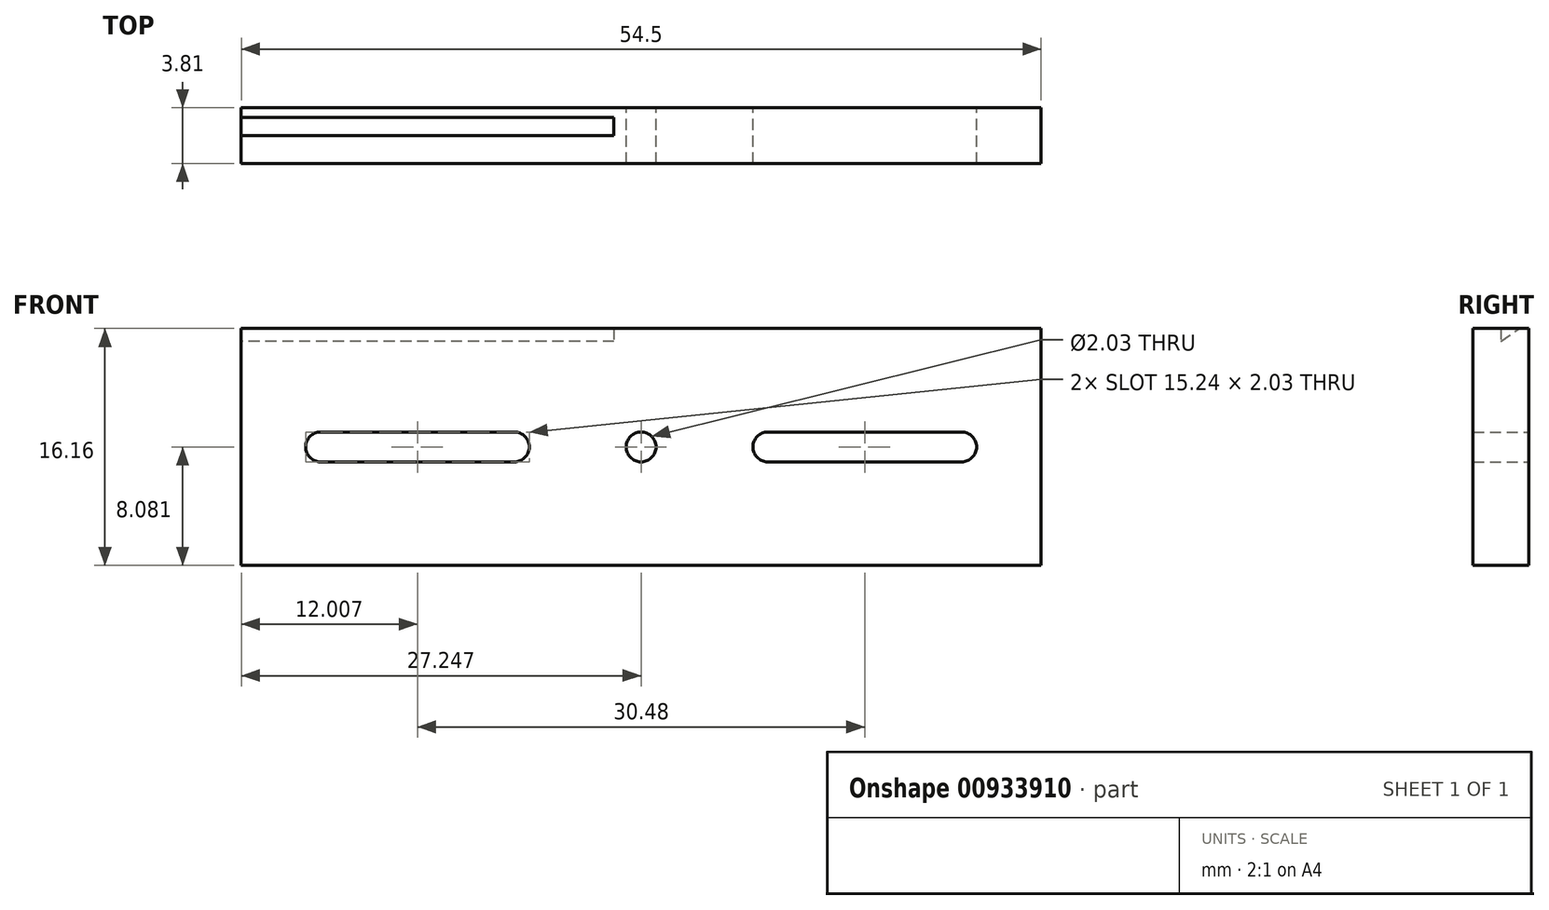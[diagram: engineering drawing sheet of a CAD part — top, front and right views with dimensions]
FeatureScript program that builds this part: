
annotation { "Feature Type Name" : "Feature", "Feature Type Description" : "" }
export const myFeature = defineFeature(function(context is Context, id is Id, definition is map)
    precondition{}
    {
        {
            var Q0;
            Q0=qCreatedBy(makeId("Front.planeOp"),FACE);
            var sketch = newSketch(context, id + "F0", { "sketchPlane" : qUnion([Q0])});
            skLineSegment(sketch, "E0", {"start": v(-28.7, 29.15) * mm, "end": v(25.8, 29.15) * mm});
            skLineSegment(sketch, "E1", {"start": v(25.8, 29.15) * mm, "end": v(25.8, 13) * mm});
            skLineSegment(sketch, "E2", {"start": v(25.8, 13) * mm, "end": v(-28.7, 13) * mm});
            skLineSegment(sketch, "E3", {"start": v(-28.7, 13) * mm, "end": v(-28.7, 29.15) * mm});
            skCircle(sketch, "E4", {"center": v(-1.45, 21.07) * mm, "radius": 1.02 * mm});
            skArc(sketch, "E5", {"start": v(-23.3, 22.09) * mm, "mid": v(-24.31, 21.07) * mm, "end": v(-23.3, 20.06) * mm});
            skArc(sketch, "E6", {"start": v(-10.09, 20.06) * mm, "mid": v(-9.07, 21.07) * mm, "end": v(-10.09, 22.09) * mm});
            skLineSegment(sketch, "E7", {"start": v(-23.3, 22.09) * mm, "end": v(-10.09, 22.09) * mm});
            skLineSegment(sketch, "E8", {"start": v(-10.09, 20.06) * mm, "end": v(-23.3, 20.06) * mm});
            skArc(sketch, "E9", {"start": v(20.4, 20.06) * mm, "mid": v(21.4, 21.07) * mm, "end": v(20.4, 22.09) * mm});
            skArc(sketch, "E10", {"start": v(7.18, 22.09) * mm, "mid": v(6.17, 21.07) * mm, "end": v(7.18, 20.06) * mm});
            skLineSegment(sketch, "E11", {"start": v(20.4, 22.09) * mm, "end": v(7.18, 22.09) * mm});
            skLineSegment(sketch, "E12", {"start": v(7.18, 20.06) * mm, "end": v(20.4, 20.06) * mm});
            skSolve(sketch);
        }
        {
            var Q0;
            Q0=makeQuery(id+"F0.imprint","IMPRINT",FACE,{"disambiguationData":[TD([[makeQuery(id+"F0.imprint","IMPRINT",EDGE,{"derivedFrom":sQuery(id+"F0.wireOp",EDGE,"E0")}),-1.0]])]});
            extrude(context, id + "F1", {"entities" : qUnion([Q0]), "depth" : 3.8 * mm, "offsetDistance" : 25.4 * mm});
        }
        {
            var Q0;
            Q0=makeQuery(id+"F1.opExtrude","SWEPT_FACE",FACE,{"disambiguationData":[OSD([sQuery(id+"F0.wireOp",EDGE,"E3")])]});
            var sketch = newSketch(context, id + "F2", { "sketchPlane" : qUnion([Q0])});
            skLineSegment(sketch, "E13", {"start": v(1.9, 29.15) * mm, "end": v(1.9, 28.29) * mm});
            skLineSegment(sketch, "E14", {"start": v(1.9, 28.29) * mm, "end": v(0.65, 29.15) * mm});
            skSolve(sketch);
        }
        {
            var Q0;
            {var subQ0=sQuery(id+"F2.wireOp",EDGE,"E13");Q0=makeQuery(id+"F2.imprint","IMPRINT",FACE,{"disambiguationData":[TD([[makeQuery(id+"F2.imprint","IMPRINT",EDGE,{"derivedFrom":subQ0}),-1.0]])]});}
            extrude(context, id + "F3", {"entities" : qUnion([Q0]), "operationType" : NewBodyOperationType.REMOVE, "oppositeDirection" : true, "depth" : 25.4 * mm, "offsetDistance" : 25.4 * mm});
        }
    });
